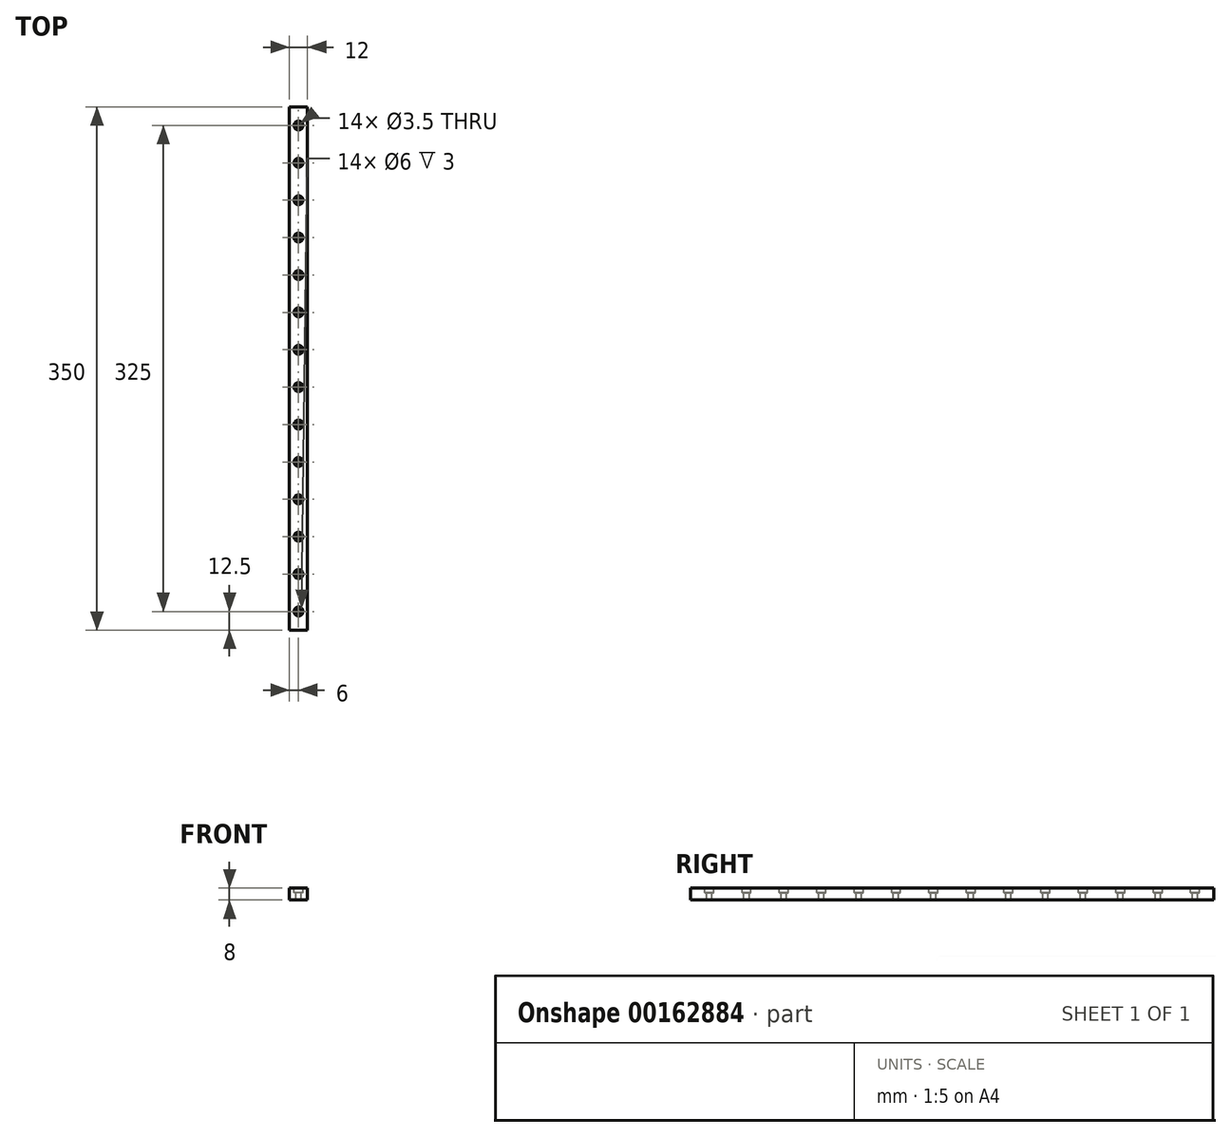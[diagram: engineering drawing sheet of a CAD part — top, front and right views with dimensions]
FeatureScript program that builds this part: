
annotation { "Feature Type Name" : "Feature", "Feature Type Description" : "" }
export const myFeature = defineFeature(function(context is Context, id is Id, definition is map)
    precondition{}
    {
        {
            var Q0;
            Q0=qCreatedBy(makeId("Front.planeOp"),FACE);
            var sketch = newSketch(context, id + "F0", { "sketchPlane" : qUnion([Q0])});
            skLineSegment(sketch, "E0.bottom", {"start": v(6, -4) * mm, "end": v(-6, -4) * mm});
            skLineSegment(sketch, "E0.top", {"start": v(6, 4) * mm, "end": v(-6, 4) * mm});
            skLineSegment(sketch, "E0.left", {"start": v(6, -4) * mm, "end": v(6, 4) * mm});
            skLineSegment(sketch, "E0.right", {"start": v(-6, -4) * mm, "end": v(-6, 4) * mm});
            skPoint(sketch, "E0.middle", {"position": v(0, 0) * mm});
            skSolve(sketch);
        }
        {
            var Q0;
            Q0=makeQuery(id+"F0.imprint","IMPRINT",FACE,{"disambiguationData":[TD([[makeQuery(id+"F0.imprint","IMPRINT",EDGE,{"derivedFrom":sQuery(id+"F0.wireOp",EDGE,"E0.bottom")}),-1.0]])]});
            extrude(context, id + "F1", {"entities" : qUnion([Q0]), "depth" : 175 * mm, "offsetDistance" : 25 * mm, "hasSecondDirection" : true, "secondDirectionOppositeDirection" : true, "secondDirectionDepth" : 175 * mm});
        }
        {
            var Q0;
            Q0=makeQuery(id+"F1.opExtrude","SWEPT_FACE",FACE,{"disambiguationData":[OSD([sQuery(id+"F0.wireOp",EDGE,"E0.top")])]});
            var sketch = newSketch(context, id + "F2", { "sketchPlane" : qUnion([Q0])});
            skPoint(sketch, "E1", {"position": v(0, -162.5) * mm});
            skPoint(sketch, "E2.0.1.0", {"position": v(0, -137.5) * mm});
            skPoint(sketch, "E2.0.2.0", {"position": v(0, -112.5) * mm});
            skPoint(sketch, "E2.0.3.0", {"position": v(0, -87.5) * mm});
            skPoint(sketch, "E2.0.4.0", {"position": v(0, -62.5) * mm});
            skPoint(sketch, "E2.0.5.0", {"position": v(0, -37.5) * mm});
            skPoint(sketch, "E2.0.6.0", {"position": v(0, -12.5) * mm});
            skPoint(sketch, "E2.0.7.0", {"position": v(0, 12.5) * mm});
            skPoint(sketch, "E2.0.8.0", {"position": v(0, 37.5) * mm});
            skPoint(sketch, "E2.0.9.0", {"position": v(0, 62.5) * mm});
            skPoint(sketch, "E2.0.10.0", {"position": v(0, 87.5) * mm});
            skPoint(sketch, "E2.0.11.0", {"position": v(0, 112.5) * mm});
            skLineSegment(sketch, "E2.direction1", {"start": v(0, -162.5) * mm, "end": v(25, -162.5) * mm, "construction": true});
            skLineSegment(sketch, "E2.direction2", {"start": v(0, -162.5) * mm, "end": v(0, -137.5) * mm, "construction": true});
            skPoint(sketch, "E3.0.0.12", {"position": v(0, 137.5) * mm});
            skPoint(sketch, "E3.0.0.13", {"position": v(0, 162.5) * mm});
            skSolve(sketch);
        }
        {
            var Q0;
            Q0=sQuery(id+"F2.wireOp",VERTEX,"E1");
            var Q1;
            Q1=sQuery(id+"F2.wireOp",VERTEX,"E2.0.1.0");
            var Q2;
            Q2=sQuery(id+"F2.wireOp",VERTEX,"E2.0.2.0");
            var Q3;
            Q3=sQuery(id+"F2.wireOp",VERTEX,"E2.0.3.0");
            var Q4;
            Q4=sQuery(id+"F2.wireOp",VERTEX,"E2.0.4.0");
            var Q5;
            Q5=sQuery(id+"F2.wireOp",VERTEX,"E2.0.5.0");
            var Q6;
            Q6=sQuery(id+"F2.wireOp",VERTEX,"E2.0.6.0");
            var Q7;
            Q7=sQuery(id+"F2.wireOp",VERTEX,"E2.0.7.0");
            var Q8;
            Q8=sQuery(id+"F2.wireOp",VERTEX,"E2.0.8.0");
            var Q9;
            Q9=sQuery(id+"F2.wireOp",VERTEX,"E2.0.9.0");
            var Q10;
            Q10=sQuery(id+"F2.wireOp",VERTEX,"E2.0.10.0");
            var Q11;
            Q11=sQuery(id+"F2.wireOp",VERTEX,"E2.0.11.0");
            var Q12;
            Q12=sQuery(id+"F2.wireOp",VERTEX,"E3.0.0.12");
            var Q13;
            Q13=sQuery(id+"F2.wireOp",VERTEX,"E3.0.0.13");
            var Q14;
            Q14=makeQuery(id+"F1.opExtrude","SWEPT_BODY",BODY,{"disambiguationData":[OSD([sQuery(id+"F0.wireOp",EDGE,"E0.bottom"),sQuery(id+"F0.wireOp",EDGE,"E0.top"),sQuery(id+"F0.wireOp",EDGE,"E0.left"),sQuery(id+"F0.wireOp",EDGE,"E0.right")])]});
            hole(context, id + "F3", {"style" : HoleStyle.C_BORE, "endStyle" : HoleEndStyle.THROUGH, "holeDiameter" : 3.5 * mm, "cBoreDiameter" : 6 * mm, "cBoreDepth" : 3 * mm, "majorDiameter" : 5 * mm, "isTappedThrough" : true, "tappedDepth" : 12 * mm, "tapClearance" : 3, "startFromSketch" : true, "locations" : qUnion([Q0, Q1, Q2, Q3, Q4, Q5, Q6, Q7, Q8, Q9, Q10, Q11, Q12, Q13]), "scope" : qUnion([Q14])});
        }
    });
